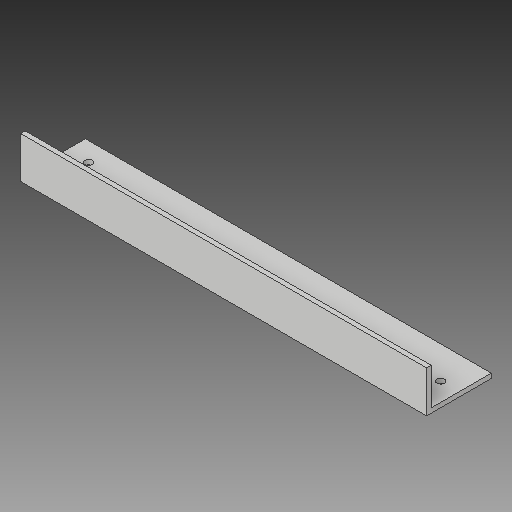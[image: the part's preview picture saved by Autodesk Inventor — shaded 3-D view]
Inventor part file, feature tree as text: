
AUTODESK INVENTOR PART (.ipt)
format: ipt  version: 2018 (Build 220112000, 112)  size: 97,792 bytes
history: native  units: in
note: dims shown in document units (in); Inventor stores cm internally (conversion verified against a paired STEP export)
features: sketch x4, other x3
ambient origin geometry x8: Origin, YZ Plane, XZ Plane, XY Plane, X Axis, Y Axis, Z Axis, Center Point
bodies: Solid1 (feature_tree)
feature tree (7):
  other  "angle iron with  holes 2_MIR.ipt"
  other  "Solid1::angle iron with  holes 2_MIR.ipt"
  other  "TaggingFeature1"
  sketch  "Sketch1"  dims[d0=0.3937in]
  sketch  "Sketch2"
  sketch  "Sketch3"
  sketch  "Sketch4"
